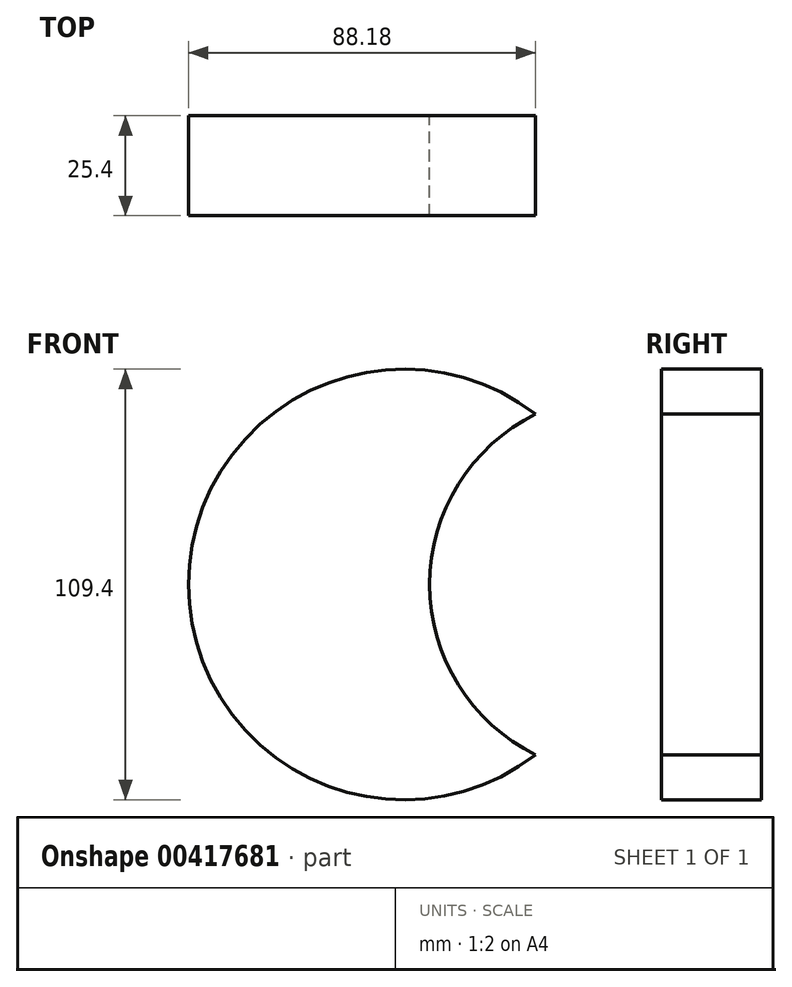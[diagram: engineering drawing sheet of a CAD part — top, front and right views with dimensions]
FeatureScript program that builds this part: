
annotation { "Feature Type Name" : "Feature", "Feature Type Description" : "" }
export const myFeature = defineFeature(function(context is Context, id is Id, definition is map)
    precondition{}
    {
        {
            var Q0;
            Q0=qCreatedBy(makeId("Front.planeOp"),FACE);
            var sketch = newSketch(context, id + "F0", { "sketchPlane" : qUnion([Q0])});
            skArc(sketch, "E0", {"start": v(33.48, 43.25) * mm, "mid": v(-54.7, 0) * mm, "end": v(33.48, -43.25) * mm});
            skArc(sketch, "E1", {"start": v(33.48, 43.25) * mm, "mid": v(6.52, 0) * mm, "end": v(33.48, -43.25) * mm});
            skSolve(sketch);
        }
        {
            var Q0;
            Q0 = qSketchRegion(id + "F0", true);
            extrude(context, id + "F1", {"entities" : qUnion([Q0]), "depth" : 25.4 * mm});
        }
    });
